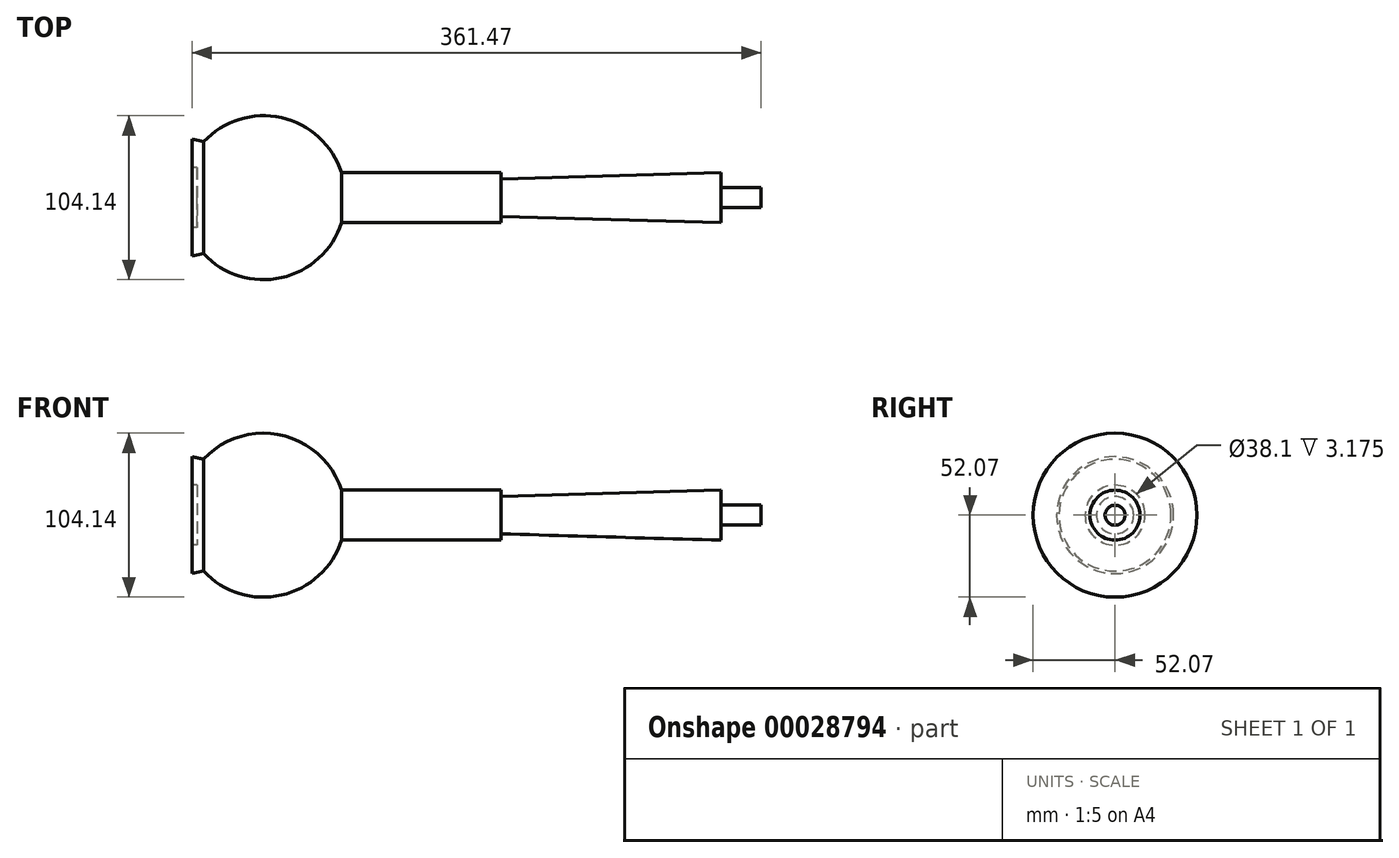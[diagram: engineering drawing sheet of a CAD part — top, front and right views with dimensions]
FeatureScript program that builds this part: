
annotation { "Feature Type Name" : "Feature", "Feature Type Description" : "" }
export const myFeature = defineFeature(function(context is Context, id is Id, definition is map)
    precondition{}
    {
        {
            var Q0;
            Q0=qCreatedBy(makeId("Front.planeOp"),FACE);
            var sketch = newSketch(context, id + "F0", { "sketchPlane" : qUnion([Q0])});
            skLineSegment(sketch, "E0", {"start": v(0, 0) * mm, "end": v(11.68, 0) * mm, "construction": true});
            skArc(sketch, "E1", {"start": v(-26.35, -35.56) * mm, "mid": v(-25.88, -36.06) * mm, "end": v(-25.4, -36.55) * mm});
            skLineSegment(sketch, "E2", {"start": v(-53.76, 35.56) * mm, "end": v(65.53, 35.56) * mm, "construction": true});
            skLineSegment(sketch, "E3", {"start": v(-61.49, -35.56) * mm, "end": v(80.65, -35.56) * mm, "construction": true});
            skLineSegment(sketch, "E4", {"start": v(0, 61.81) * mm, "end": v(0, -41.35) * mm, "construction": true});
            skLineSegment(sketch, "E5", {"start": v(-25.4, 64.85) * mm, "end": v(-25.4, -82.76) * mm, "construction": true});
            skLineSegment(sketch, "E6", {"start": v(-26.35, 35.56) * mm, "end": v(-33.8, 37.14) * mm});
            skLineSegment(sketch, "E7", {"start": v(-26.35, -35.56) * mm, "end": v(-33.8, -37.14) * mm});
            skLineSegment(sketch, "E8", {"start": v(-33.8, 37.14) * mm, "end": v(-33.8, 0) * mm});
            skArc(sketch, "E9.trimOffspring", {"start": v(0.25, 50.8) * mm, "mid": v(0.13, 50.8) * mm, "end": v(0, 50.8) * mm});
            skLineSegment(sketch, "E10", {"start": v(0, 0) * mm, "end": v(-33.8, 0) * mm, "construction": true});
            skLineSegment(sketch, "E11", {"start": v(-33.8, 0) * mm, "end": v(63.75, 0) * mm});
            skLineSegment(sketch, "E12.trimOffspring", {"start": v(-33.8, -35.56) * mm, "end": v(-33.8, -37.14) * mm});
            skArc(sketch, "E13.trimOffspring", {"start": v(63.75, 0) * mm, "mid": v(30.8, 48.43) * mm, "end": v(-26.35, 35.56) * mm});
            skSolve(sketch);
        }
        {
            var Q0;
            {var subQ2=sQuery(id+"F0.wireOp",EDGE,"E6");Q0=makeQuery(id+"F0.imprint","IMPRINT",FACE,{"disambiguationData":[TD([[makeQuery(id+"F0.imprint","IMPRINT",EDGE,{"derivedFrom":subQ2}),1.0]])]});}
            var Q1;
            Q1=sQuery(id+"F0.wireOp",EDGE,"E11");
            revolve(context, id + "F1", {"entities" : qUnion([Q0]), "axis" : qUnion([Q1]), "revolveType" : RevolveType.FULL});
        }
        {
            var Q0;
            Q0=makeQuery(id+"F1.opRevolve","SWEPT_FACE",FACE,{"disambiguationData":[OSD([sQuery(id+"F0.wireOp",EDGE,"E8")])]});
            var sketch = newSketch(context, id + "F2", { "sketchPlane" : qUnion([Q0])});
            skCircle(sketch, "E14", {"center": v(0, 0) * mm, "radius": 19.05 * mm});
            skSolve(sketch);
        }
        {
            var Q0;
            Q0=makeQuery(id+"F2.imprint","IMPRINT",FACE,{"disambiguationData":[TD([[makeQuery(id+"F2.imprint","IMPRINT",EDGE,{"derivedFrom":sQuery(id+"F2.wireOp",EDGE,"E14")}),1.0]])]});
            extrude(context, id + "F3", {"entities" : qUnion([Q0]), "operationType" : NewBodyOperationType.REMOVE, "oppositeDirection" : true, "depth" : 3.17 * mm});
        }
        {
            var Q0;
            Q0=qCreatedBy(makeId("Right.planeOp"),FACE);
            cPlane(context, id + "F4", {"entities" : qUnion([Q0]), "cplaneType" : CPlaneType.OFFSET, "offset" : 60.96 * mm, "width" : 152.4 * mm, "height" : 152.4 * mm});
        }
        {
            var Q0;
            Q0=qCreatedBy(id+"F4.planeOp",FACE);
            var sketch = newSketch(context, id + "F5", { "sketchPlane" : qUnion([Q0])});
            skCircle(sketch, "E15", {"center": v(0, 0) * mm, "radius": 15.88 * mm});
            skSolve(sketch);
        }
        {
            var Q0;
            Q0=makeQuery(id+"F5.imprint","IMPRINT",FACE,{"disambiguationData":[TD([[makeQuery(id+"F5.imprint","IMPRINT",EDGE,{"derivedFrom":sQuery(id+"F5.wireOp",EDGE,"E15")}),1.0]])]});
            extrude(context, id + "F6", {"entities" : qUnion([Q0]), "operationType" : NewBodyOperationType.ADD, "depth" : 101.6 * mm});
        }
        {
            var Q0;
            Q0=makeQuery(id+"F6.opExtrude","CAP_FACE",FACE,{"disambiguationData":[OSD([sQuery(id+"F5.wireOp",EDGE,"E15")])],"isStart":false});
            var sketch = newSketch(context, id + "F7", { "sketchPlane" : qUnion([Q0])});
            skCircle(sketch, "E16", {"center": v(0, 0) * mm, "radius": 11.87 * mm});
            skSolve(sketch);
        }
        {
            var Q0;
            Q0=makeQuery(id+"F7.imprint","IMPRINT",FACE,{"disambiguationData":[TD([[makeQuery(id+"F7.imprint","IMPRINT",EDGE,{"derivedFrom":sQuery(id+"F7.wireOp",EDGE,"E16")}),1.0]])]});
            cPlane(context, id + "F8", {"entities" : qUnion([Q0]), "cplaneType" : CPlaneType.OFFSET, "offset" : 139.7 * mm, "width" : 152.4 * mm, "height" : 152.4 * mm});
        }
        {
            var Q0;
            Q0=qCreatedBy(id+"F8.planeOp",FACE);
            var sketch = newSketch(context, id + "F9", { "sketchPlane" : qUnion([Q0])});
            skCircle(sketch, "E17", {"center": v(0, 0) * mm, "radius": 15.88 * mm});
            skSolve(sketch);
        }
        {
            var Q1;
            Q1=makeQuery(id+"F7.imprint","IMPRINT",FACE,{"disambiguationData":[TD([[makeQuery(id+"F7.imprint","IMPRINT",EDGE,{"derivedFrom":sQuery(id+"F7.wireOp",EDGE,"E16")}),1.0]])]});
            var Q2;
            Q2=makeQuery(id+"F9.imprint","IMPRINT",FACE,{"disambiguationData":[TD([[makeQuery(id+"F9.imprint","IMPRINT",EDGE,{"derivedFrom":sQuery(id+"F9.wireOp",EDGE,"E17")}),1.0]])]});
            loft(context, id + "F10", {"operationType" : NewBodyOperationType.ADD, "sheetProfilesArray" : [{ "sheetProfileEntities" : qUnion([Q1]) }, { "sheetProfileEntities" : qUnion([Q2]) }]});
        }
        {
            var Q0;
            Q0=makeQuery(id+"F10.opLoft","CAP_FACE",FACE,{"disambiguationData":[OSD([makeQuery(id+"F9.imprint","IMPRINT",FACE,{"disambiguationData":[TD([[makeQuery(id+"F9.imprint","IMPRINT",EDGE,{"derivedFrom":sQuery(id+"F9.wireOp",EDGE,"E17")}),1.0]])]})])],"isStart":true});
            var sketch = newSketch(context, id + "F11", { "sketchPlane" : qUnion([Q0])});
            skCircle(sketch, "E18", {"center": v(0, 0) * mm, "radius": 6.35 * mm});
            skSolve(sketch);
        }
        {
            var Q0;
            Q0=makeQuery(id+"F11.imprint","IMPRINT",FACE,{"disambiguationData":[TD([[makeQuery(id+"F11.imprint","IMPRINT",EDGE,{"derivedFrom":sQuery(id+"F11.wireOp",EDGE,"E18")}),1.0]])]});
            extrude(context, id + "F12", {"entities" : qUnion([Q0]), "operationType" : NewBodyOperationType.ADD, "depth" : 25.4 * mm});
        }
    });
